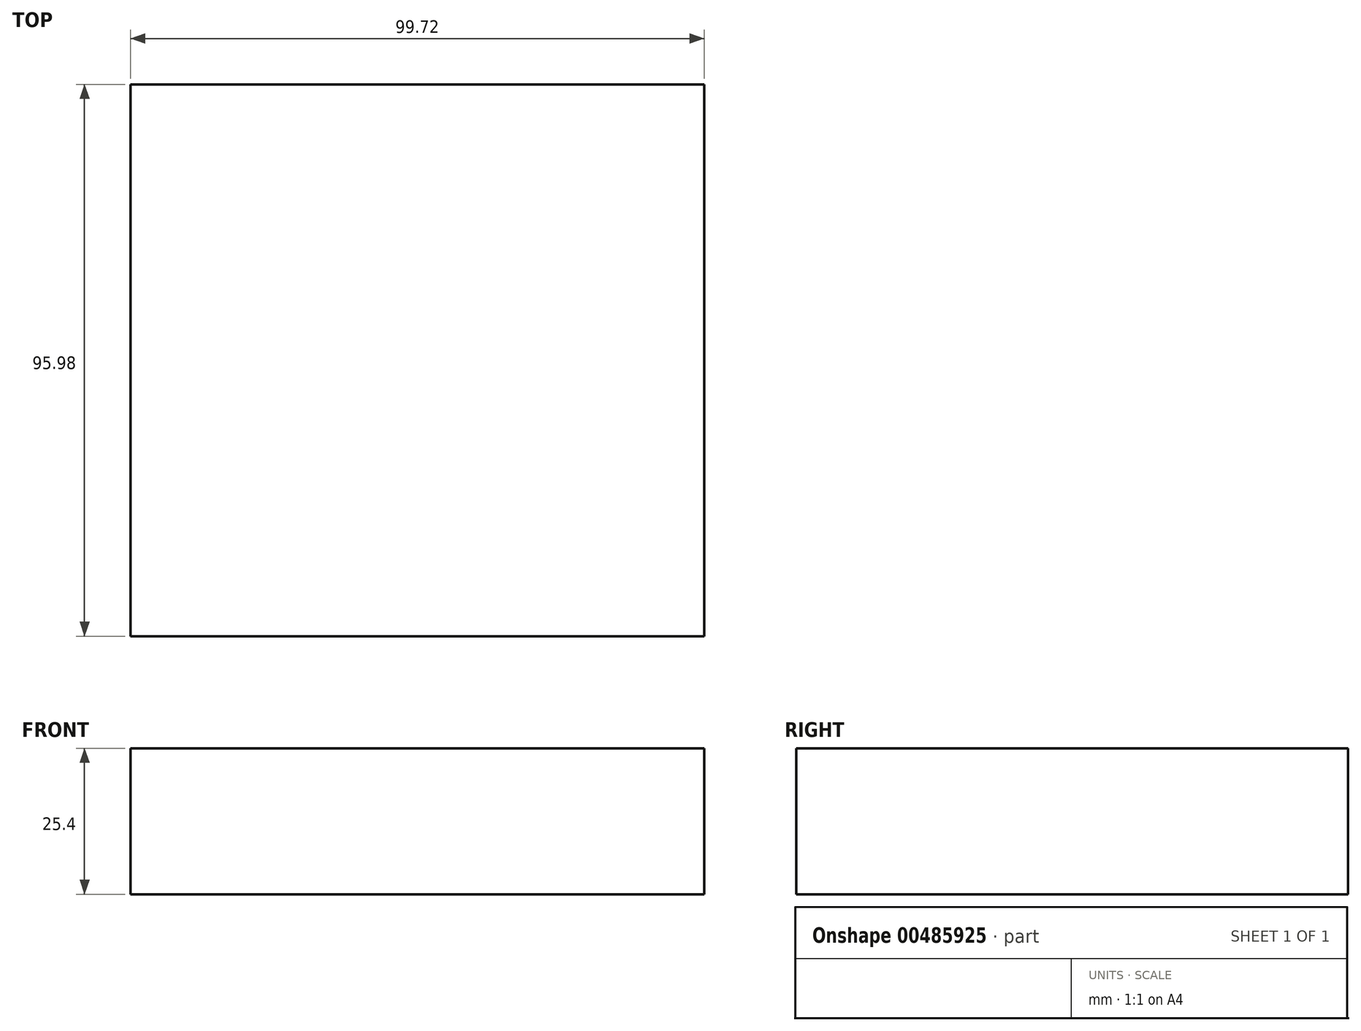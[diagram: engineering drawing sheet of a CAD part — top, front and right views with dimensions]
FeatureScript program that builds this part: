
annotation { "Feature Type Name" : "Feature", "Feature Type Description" : "" }
export const myFeature = defineFeature(function(context is Context, id is Id, definition is map)
    precondition{}
    {
        {
            var Q0;
            Q0=qCreatedBy(makeId("Top.planeOp"),FACE);
            var sketch = newSketch(context, id + "F0", { "sketchPlane" : qUnion([Q0])});
            skLineSegment(sketch, "E0.bottom", {"start": v(-49.86, 53.7) * mm, "end": v(49.86, 53.7) * mm});
            skLineSegment(sketch, "E0.top", {"start": v(-49.86, -42.28) * mm, "end": v(49.86, -42.28) * mm});
            skLineSegment(sketch, "E0.left", {"start": v(-49.86, 53.7) * mm, "end": v(-49.86, -42.28) * mm});
            skLineSegment(sketch, "E0.right", {"start": v(49.86, 53.7) * mm, "end": v(49.86, -42.28) * mm});
            skSolve(sketch);
        }
        {
            var Q0;
            Q0 = qSketchRegion(id + "F0", true);
            var Q1;
            Q1=makeQuery(id+"F0.imprint","IMPRINT",FACE,{"disambiguationData":[TD([[makeQuery(id+"F0.imprint","IMPRINT",EDGE,{"derivedFrom":sQuery(id+"F0.wireOp",EDGE,"E0.bottom")}),-1.0]])]});
            extrude(context, id + "F1", {"entities" : qUnion([Q0, Q1]), "depth" : 25.4 * mm});
        }
    });
